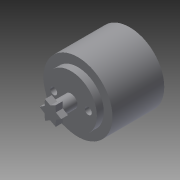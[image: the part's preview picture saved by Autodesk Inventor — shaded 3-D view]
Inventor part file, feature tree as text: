
AUTODESK INVENTOR PART (.ipt)
format: ipt  version: 2015 (Build 190159000, 159)  size: 153,600 bytes
history: native  units: in
note: dims shown in document units (in); Inventor stores cm internally (conversion verified against a paired STEP export)
features: sketch x6, extrude x5, plane x1, hole x1
ambient origin geometry x8: Origin, YZ Plane, XZ Plane, XY Plane, X Axis, Y Axis, Z Axis, Center Point
bodies: Solid1 (feature_tree)
feature tree (13):
  extrude  "Extrusion1"  Depth=0.75in TaperAngle=0.0deg
  extrude  "Extrusion2"  Depth=0.05in TaperAngle=0.0deg
  extrude  "Extrusion3"  Depth=0.05in TaperAngle=0.0deg
  extrude  "Extrusion4"  TaperAngle=0.0deg  [1 undecoded]
  plane  "Work Plane1"
  extrude  "Extrusion10"  Depth=0.3125in
  hole  "Hole1"  [1 undecoded]
  sketch  "Sketch1"  dims[d0=1.0in d1=0.75in d2=0.0in]
  sketch  "Sketch2"  dims[d3=0.75in d4=0.05in d5=0.0in]
  sketch  "Sketch3"  dims[d6=0.75in d7=0.05in d8=0.0in]
  sketch  "Sketch4"  dims[d9=0.2in d10=0.0in d11=0.0in]
  sketch  "Sketch10"  dims[d26=0.1875in d27=0.3125in]
  sketch  "Sketch11"  dims[d28=2.3622in d30=360.0deg d32=2.3622in d34=360.0deg d36=2.3622in d38=360.0deg d40=2.3622in d42=360.0deg d44=0.1in d45=0.0in d46=0.25in d47=0.25in d48=0.1in d49=0.75in d50=0.375in d51=0.25in d52=0.5635in d53=0.5in d54=0.8108in]
note: 2 required parameter values undecoded (feature->parameter linkage not recoverable at this tier; creation-order binding heuristic only, values carry confidence <= 0.55)
